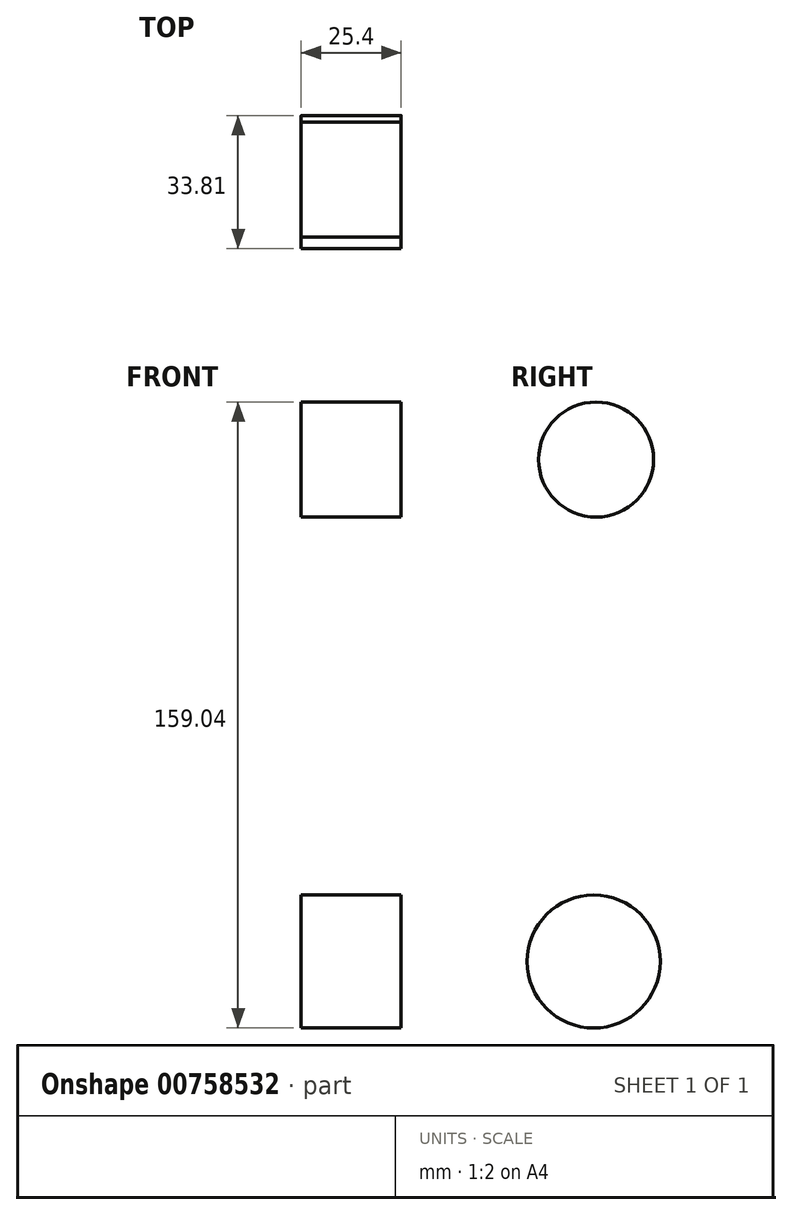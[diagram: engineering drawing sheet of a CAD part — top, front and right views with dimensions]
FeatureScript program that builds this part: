
annotation { "Feature Type Name" : "Feature", "Feature Type Description" : "" }
export const myFeature = defineFeature(function(context is Context, id is Id, definition is map)
    precondition{}
    {
        {
            var Q0;
            Q0=qCreatedBy(makeId("Right.planeOp"),FACE);
            var sketch = newSketch(context, id + "F0", { "sketchPlane" : qUnion([Q0])});
            skLineSegment(sketch, "E0", {"start": v(37.8, 23.01) * mm, "end": v(17.68, 52.27) * mm});
            skLineSegment(sketch, "E1", {"start": v(17.68, 52.27) * mm, "end": v(17.68, 87.93) * mm});
            skLineSegment(sketch, "E2", {"start": v(17.68, 87.93) * mm, "end": v(-15.55, 87.93) * mm});
            skLineSegment(sketch, "E3", {"start": v(-15.55, 87.93) * mm, "end": v(-15.55, 69.5) * mm});
            skLineSegment(sketch, "E4", {"start": v(17.68, 52.27) * mm, "end": v(40.63, 29.33) * mm});
            skLineSegment(sketch, "E5", {"start": v(40.63, 29.33) * mm, "end": v(40.63, -49.5) * mm});
            skLineSegment(sketch, "E6", {"start": v(40.63, -49.5) * mm, "end": v(17.68, -71.24) * mm});
            skLineSegment(sketch, "E7", {"start": v(17.68, -71.24) * mm, "end": v(17.68, -102.05) * mm});
            skLineSegment(sketch, "E8", {"start": v(17.68, -102.05) * mm, "end": v(-15.55, -102.05) * mm});
            skLineSegment(sketch, "E9", {"start": v(-15.55, -102.05) * mm, "end": v(-15.55, -71.24) * mm});
            skCircle(sketch, "E10", {"center": v(-15.55, 69.5) * mm, "radius": 14.61 * mm});
            skSolve(sketch);
        }
        {
            var Q0;
            Q0=qCreatedBy(makeId("Right.planeOp"),FACE);
            var sketch = newSketch(context, id + "F1", { "sketchPlane" : qUnion([Q0])});
            skLineSegment(sketch, "E11", {"start": v(-15.41, 54.11) * mm, "end": v(-15.41, -44.43) * mm});
            skCircle(sketch, "E12", {"center": v(-16.17, -58.03) * mm, "radius": 16.9 * mm});
            skLineSegment(sketch, "E13", {"start": v(40.43, -4.37) * mm, "end": v(-15.41, -4.37) * mm});
            skLineSegment(sketch, "E14", {"start": v(35.92, -10.53) * mm, "end": v(15.81, -10.53) * mm});
            skLineSegment(sketch, "E15", {"start": v(15.81, -10.53) * mm, "end": v(15.81, -54.44) * mm});
            skLineSegment(sketch, "E16", {"start": v(15.81, -54.44) * mm, "end": v(33.87, -41.3) * mm});
            skLineSegment(sketch, "E17", {"start": v(35.92, -10.53) * mm, "end": v(35.92, -41.3) * mm});
            skLineSegment(sketch, "E18", {"start": v(35.92, 6.7) * mm, "end": v(15.81, 6.7) * mm});
            skLineSegment(sketch, "E19", {"start": v(35.92, 6.7) * mm, "end": v(35.92, 27.64) * mm});
            skLineSegment(sketch, "E20", {"start": v(35.92, 27.64) * mm, "end": v(15.81, 46.1) * mm});
            skLineSegment(sketch, "E21", {"start": v(15.81, 46.1) * mm, "end": v(15.81, 6.7) * mm});
            skSolve(sketch);
        }
        {
            var Q0;
            Q0=makeQuery(id+"F1.imprint","IMPRINT",FACE,{"disambiguationData":[TD([[makeQuery(id+"F1.imprint","IMPRINT",EDGE,{"derivedFrom":sQuery(id+"F1.wireOp",EDGE,"E12")}),1.0]])]});
            extrude(context, id + "F2", {"entities" : qUnion([Q0]), "depth" : 25.4 * mm, "offsetDistance" : 25.4 * mm});
        }
        {
            var Q0;
            Q0=makeQuery(id+"F0.imprint","IMPRINT",FACE,{"disambiguationData":[TD([[makeQuery(id+"F0.imprint","IMPRINT",EDGE,{"derivedFrom":sQuery(id+"F0.wireOp",EDGE,"E10")}),1.0]])]});
            extrude(context, id + "F3", {"entities" : qUnion([Q0]), "depth" : 25.4 * mm, "offsetDistance" : 25.4 * mm});
        }
    });
